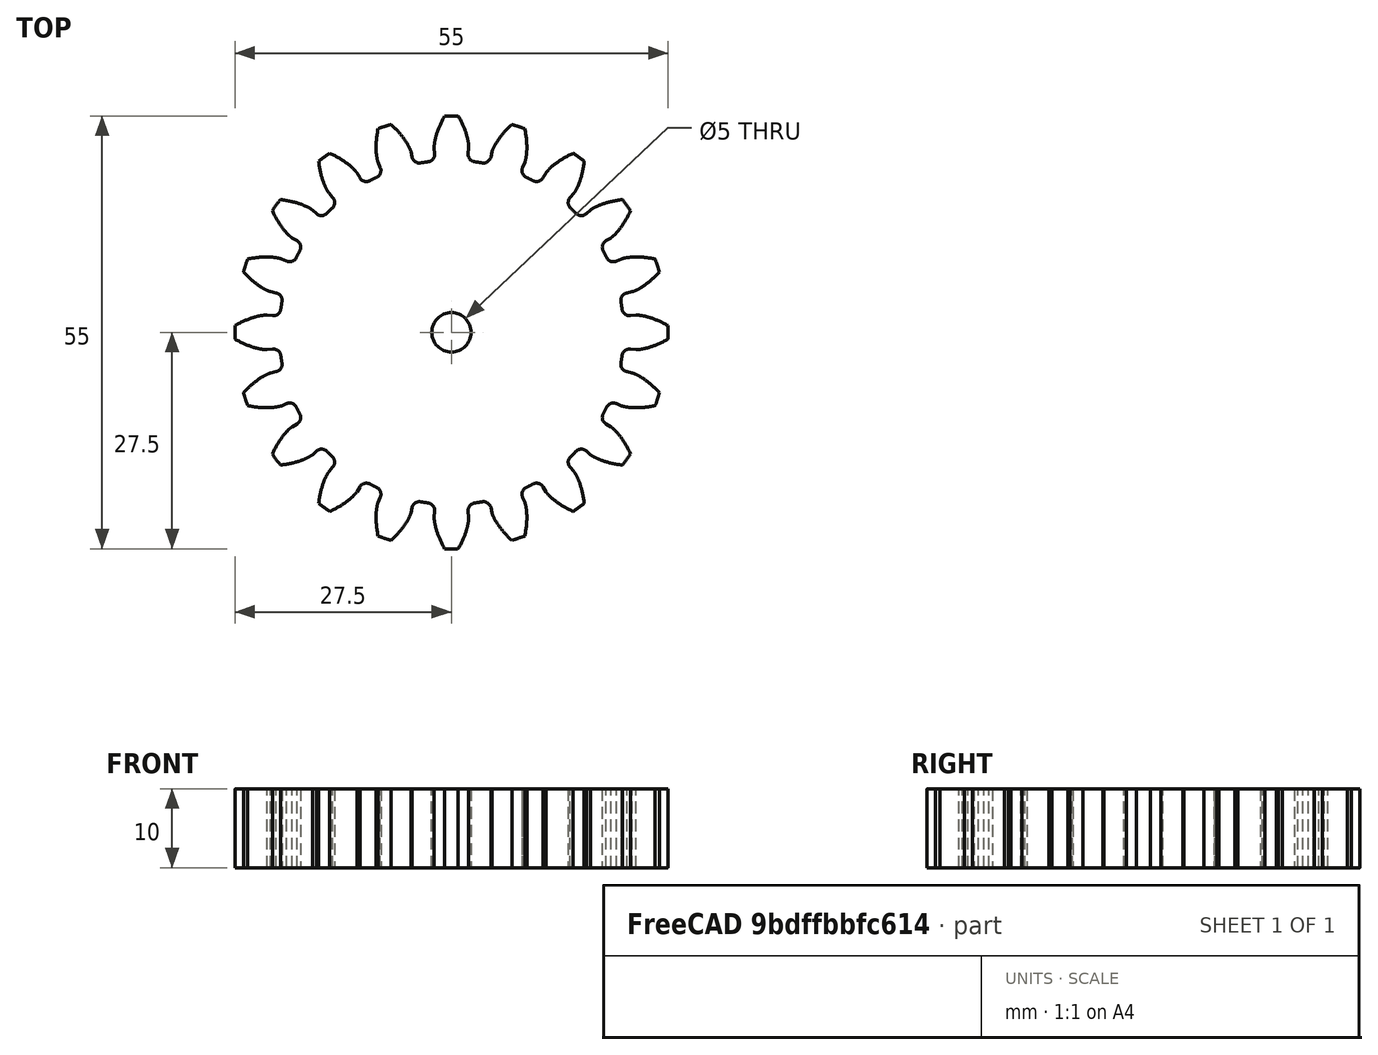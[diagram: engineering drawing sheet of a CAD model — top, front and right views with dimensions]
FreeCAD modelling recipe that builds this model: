
FCSTD DOCUMENT  (FreeCAD 1.0R39109 (Git))
Label: ギヤ50mm
License: All rights reserved
LicenseURL: https://en.wikipedia.org/wiki/All_rights_reserved
objects: Part::Part2DObjectPython×1, PartDesign::Pad×1, Sketcher::SketchObject×1, PartDesign::Pocket×1, PartDesign::Body×1
note: 10 computed .brp shape members not serialized (recipe doc carries the construction recipe); baked Part::Feature solids carry a one-line shape summary decoded from their .brp

FEATURE [Part::Part2DObjectPython] InvoluteGear  # Draft 2D object (typed FeaturePython)
  AddendumCoefficient = 1
  DedendumCoefficient = 1.25
  ExternalGear = true
  HighPrecision = true
  Modules = 2.5
  NumberOfTeeth = 20
  PressureAngle = 20
  ProfileShiftCoefficient = 0
  RootFilletCoefficient = 0.38
FEATURE [PartDesign::Pad] Pad
  Direction = (0,0,1)
  Length = 10
  Length2 = 10
  Profile = -> InvoluteGear
  ReferenceAxis = -> InvoluteGear [N_Axis]
  Refine = true
  Suppressed = false
  Type = 0
FEATURE [Sketcher::SketchObject] Sketch
  ArcFitTolerance = 1e-06
  AttachmentSupport = -> [Pad]
  FullyConstrained = true
  MakeInternals = false
  MapMode = 5
  Placement = pos=(0,0,10) rot=(0,0,1;0rad)
  sketch-geometry (1):
    g0: Circle CenterX=0 CenterY=0 CenterZ=0 NormalX=0 NormalY=0 NormalZ=1 AngleXU=0 Radius=2.5
  constraints (2):
    c: Coincident(g0,g-1)
    c: Diameter(g0) = 5
FEATURE [PartDesign::Pocket] Pocket
  BaseFeature = -> Pad
  Direction = (0,0,-1)
  Length = 5
  Length2 = 5
  Profile = -> Sketch
  ReferenceAxis = -> Sketch [N_Axis]
  Refine = true
  Suppressed = false
  Type = 1
FEATURE [PartDesign::Body] Body
  AllowCompound = false
  Group = -> [InvoluteGear,Pad,Sketch,Pocket]
  Origin = -> Origin
  Tip = -> Pocket
